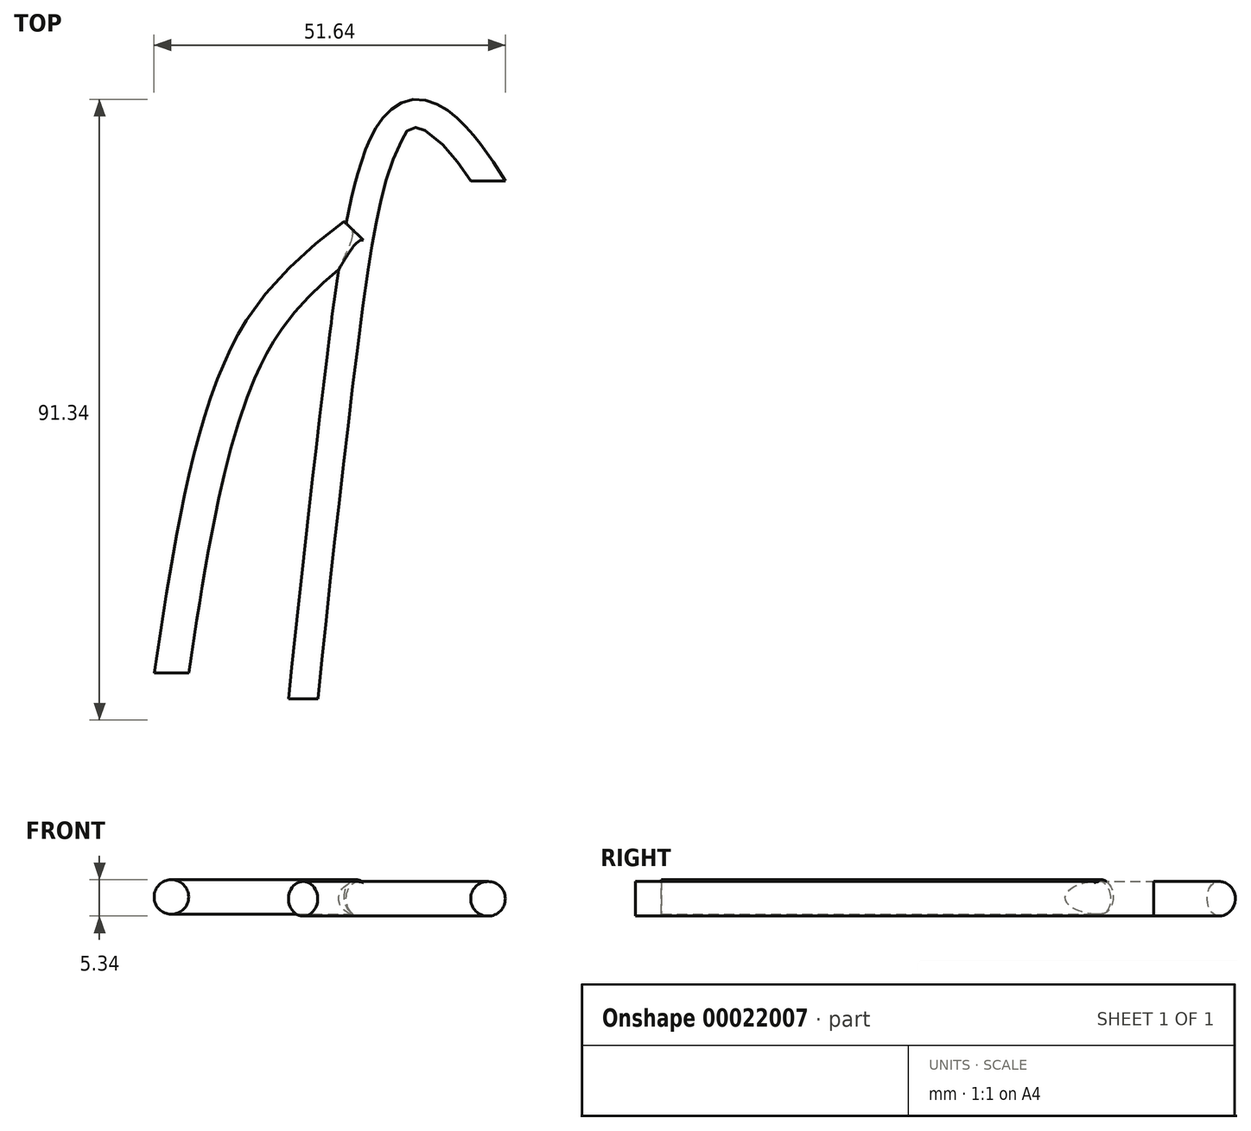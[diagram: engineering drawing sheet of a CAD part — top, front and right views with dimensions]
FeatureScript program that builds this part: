
annotation { "Feature Type Name" : "Feature", "Feature Type Description" : "" }
export const myFeature = defineFeature(function(context is Context, id is Id, definition is map)
    precondition{}
    {
        {
            var Q0;
            Q0=qCreatedBy(makeId("Top.planeOp"),FACE);
            var sketch = newSketch(context, id + "F0", { "sketchPlane" : qUnion([Q0])});
            skFitSpline(sketch, "E0", {"points": [v(0, 0) * mm, v(-21.68, -27.24) * mm, v(-45.64, -424.33) * mm], "startDerivative": vector(-197.47, 310.29) * mm, "endDerivative": vector(-6.39, -667.07) * mm});
            skFitSpline(sketch, "E1", {"points": [v(-18.92, -7.73) * mm, v(-34.56, -24.4) * mm, v(-46.25, -72.1) * mm], "startDerivative": vector(-42.71, -33.06) * mm, "endDerivative": vector(-14, -91.94) * mm});
            skSolve(sketch);
        }
        {
            var Q0;
            Q0=qCreatedBy(makeId("Front.planeOp"),FACE);
            var sketch = newSketch(context, id + "F1", { "sketchPlane" : qUnion([Q0])});
            skCircle(sketch, "E2", {"center": v(0, 0) * mm, "radius": 2.54 * mm});
            skSolve(sketch);
        }
        {
            var Q0;
            Q0=makeQuery(id+"F1.imprint","IMPRINT",FACE,{"disambiguationData":[TD([[makeQuery(id+"F1.imprint","IMPRINT",EDGE,{"derivedFrom":sQuery(id+"F1.wireOp",EDGE,"E2")}),1.0]])]});
            var Q1;
            Q1=sQuery(id+"F0.wireOp",EDGE,"E0");
            sweep(context, id + "F2", {"profiles" : qUnion([Q0]), "path" : qUnion([Q1])});
        }
        {
            var Q0;
            Q0=makeQuery(id+"F2.opSweep","CAP_FACE",FACE,{"disambiguationData":[OSD([sQuery(id+"F0.wireOp",VERTEX,"E0.end"),sQuery(id+"F1.wireOp",EDGE,"E2")])],"isStart":false});
            extrude(context, id + "F3", {"entities" : qUnion([Q0]), "operationType" : NewBodyOperationType.REMOVE, "oppositeDirection" : true, "depth" : 25.4 * mm});
        }
        {
            var Q0;
            Q0=qCreatedBy(makeId("Front.planeOp"),FACE);
            cPlane(context, id + "F4", {"entities" : qUnion([Q0]), "cplaneType" : CPlaneType.OFFSET, "offset" : 152.4 * mm, "width" : 152.4 * mm, "height" : 152.4 * mm});
        }
        {
            var Q0;
            Q0=qCreatedBy(id+"F4.planeOp",FACE);
            var sketch = newSketch(context, id + "F5", { "sketchPlane" : qUnion([Q0])});
            skCircle(sketch, "E3", {"center": v(-5.08, -0.92) * mm, "radius": 82.53 * mm});
            skSolve(sketch);
        }
        {
            var Q0;
            Q0 = qSketchRegion(id + "F5", true);
            extrude(context, id + "F6", {"entities" : qUnion([Q0]), "operationType" : NewBodyOperationType.REMOVE, "depth" : 369.5 * mm});
        }
        {
            var Q0;
            Q0 = qSketchRegion(id + "F5", true);
            extrude(context, id + "F7", {"entities" : qUnion([Q0]), "operationType" : NewBodyOperationType.REMOVE, "oppositeDirection" : true, "depth" : 76.2 * mm});
        }
        {
            var Q0;
            Q0=qCreatedBy(id+"F4.planeOp",FACE);
            cPlane(context, id + "F8", {"entities" : qUnion([Q0]), "cplaneType" : CPlaneType.OFFSET, "offset" : 80 * mm, "oppositeDirection" : true, "width" : 152.4 * mm, "height" : 152.4 * mm});
        }
        {
            var Q0;
            Q0=qCreatedBy(id+"F8.planeOp",FACE);
            var sketch = newSketch(context, id + "F9", { "sketchPlane" : qUnion([Q0])});
            skCircle(sketch, "E4", {"center": v(-46.56, 0.26) * mm, "radius": 2.54 * mm});
            skSolve(sketch);
        }
        {
            var Q0;
            Q0=makeQuery(id+"F9.imprint","IMPRINT",FACE,{"disambiguationData":[TD([[makeQuery(id+"F9.imprint","IMPRINT",EDGE,{"derivedFrom":sQuery(id+"F9.wireOp",EDGE,"E4")}),1.0]])]});
            var Q1;
            Q1=sQuery(id+"F0.wireOp",EDGE,"E1");
            sweep(context, id + "F10", {"operationType" : NewBodyOperationType.ADD, "profiles" : qUnion([Q0]), "path" : qUnion([Q1])});
        }
    });
